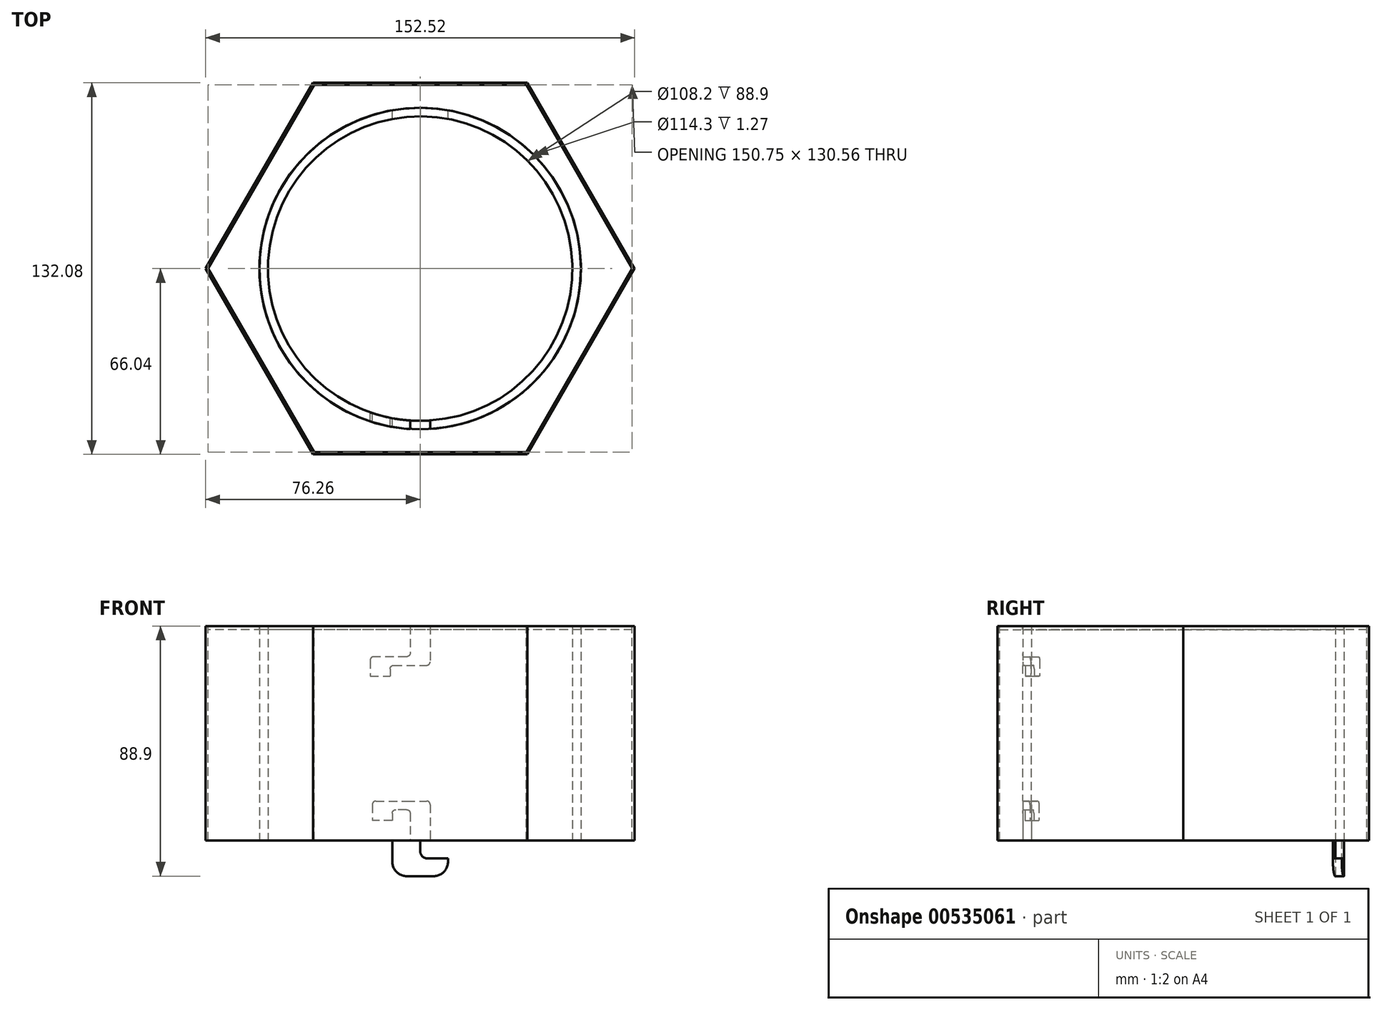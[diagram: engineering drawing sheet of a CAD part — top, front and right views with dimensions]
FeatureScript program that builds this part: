
annotation { "Feature Type Name" : "Feature", "Feature Type Description" : "" }
export const myFeature = defineFeature(function(context is Context, id is Id, definition is map)
    precondition{}
    {
        {
            var Q0;
            Q0=qCreatedBy(makeId("Top.planeOp"),FACE);
            var sketch = newSketch(context, id + "F0", { "sketchPlane" : qUnion([Q0])});
            skCircle(sketch, "E0", {"center": v(0, 0) * mm, "radius": 54.1 * mm});
            skCircle(sketch, "E1", {"center": v(0, 0) * mm, "radius": 57.15 * mm});
            skSolve(sketch);
        }
        {
            var Q0;
            Q0=qSketchRegion(id+"F0",true);
            extrude(context, id + "F1", {"entities" : qUnion([Q0]), "depth" : 76.2 * mm, "offsetDistance" : 25.4 * mm, "symmetric" : true});
        }
        {
            var Q0;
            Q0=qCreatedBy(makeId("Front.planeOp"),FACE);
            var sketch = newSketch(context, id + "F2", { "sketchPlane" : qUnion([Q0])});
            skLineSegment(sketch, "E2", {"start": v(-3.56, -38.1) * mm, "end": v(-3.56, -27.18) * mm});
            skLineSegment(sketch, "E3", {"start": v(-3.56, -27.18) * mm, "end": v(-9.9, -27.18) * mm});
            skLineSegment(sketch, "E4", {"start": v(-9.9, -27.18) * mm, "end": v(-9.9, -30.99) * mm});
            skLineSegment(sketch, "E5", {"start": v(-9.9, -30.99) * mm, "end": v(-17.02, -30.99) * mm});
            skLineSegment(sketch, "E6", {"start": v(-17.02, -30.99) * mm, "end": v(-17.02, -24.13) * mm});
            skLineSegment(sketch, "E7", {"start": v(-17.02, -24.13) * mm, "end": v(3.56, -24.13) * mm});
            skLineSegment(sketch, "E8", {"start": v(3.56, -24.13) * mm, "end": v(3.56, -38.1) * mm});
            skPoint(sketch, "E9", {"position": v(0, -38.1) * mm});
            skPoint(sketch, "E10", {"position": v(3.56, -38.1) * mm});
            skPoint(sketch, "E11", {"position": v(-3.56, -38.1) * mm});
            skLineSegment(sketch, "E12", {"start": v(-3.56, -38.1) * mm, "end": v(3.56, -38.1) * mm});
            skPoint(sketch, "E13.MirrorP", {"position": v(-3.56, 38.1) * mm});
            skLineSegment(sketch, "E14.MirrorCS", {"start": v(-3.56, 38.1) * mm, "end": v(3.56, 38.1) * mm});
            skLineSegment(sketch, "E15.MirrorCS", {"start": v(3.56, 24.13) * mm, "end": v(3.56, 38.1) * mm});
            skLineSegment(sketch, "E16.MirrorCS", {"start": v(-3.56, 38.1) * mm, "end": v(-3.56, 27.18) * mm});
            skLineSegment(sketch, "E17", {"start": v(-3.56, 27.18) * mm, "end": v(-17.78, 27.18) * mm});
            skLineSegment(sketch, "E18", {"start": v(-17.78, 27.18) * mm, "end": v(-17.78, 20.32) * mm});
            skLineSegment(sketch, "E19", {"start": v(-17.78, 20.32) * mm, "end": v(-10.67, 20.32) * mm});
            skLineSegment(sketch, "E20", {"start": v(-10.67, 20.32) * mm, "end": v(-10.67, 24.13) * mm});
            skLineSegment(sketch, "E21", {"start": v(-10.67, 24.13) * mm, "end": v(3.56, 24.13) * mm});
            skSolve(sketch);
        }
        {
            var Q0;
            Q0=qSketchRegion(id+"F2",true);
            extrude(context, id + "F3", {"entities" : qUnion([Q0]), "operationType" : NewBodyOperationType.REMOVE, "depth" : 133.86 * mm, "offsetDistance" : 25.4 * mm});
        }
        {
            var Q0;
            Q0=makeQuery(id+"F3.boolean.opBoolean","COPY",EDGE,{"derivedFrom":makeQuery(id+"F3.opExtrude","SWEPT_EDGE",EDGE,{"disambiguationData":[OSD([sQuery(id+"F2.wireOp",EDGE,"E3"),sQuery(id+"F2.wireOp",EDGE,"E4")])]})});
            var Q1;
            Q1=makeQuery(id+"F3.boolean.opBoolean","COPY",EDGE,{"derivedFrom":makeQuery(id+"F3.opExtrude","SWEPT_EDGE",EDGE,{"disambiguationData":[OSD([sQuery(id+"F2.wireOp",EDGE,"E2"),sQuery(id+"F2.wireOp",EDGE,"E3")])]})});
            var Q2;
            Q2=makeQuery(id+"F3.boolean.opBoolean","COPY",EDGE,{"derivedFrom":makeQuery(id+"F3.opExtrude","SWEPT_EDGE",EDGE,{"disambiguationData":[OSD([sQuery(id+"F2.wireOp",EDGE,"E7"),sQuery(id+"F2.wireOp",EDGE,"E8")])]})});
            var Q3;
            Q3=makeQuery(id+"F3.boolean.opBoolean","COPY",EDGE,{"derivedFrom":makeQuery(id+"F3.opExtrude","SWEPT_EDGE",EDGE,{"disambiguationData":[OSD([sQuery(id+"F2.wireOp",EDGE,"E6"),sQuery(id+"F2.wireOp",EDGE,"E7")])]})});
            fillet(context, id + "F4", {"entities" : qUnion([Q0, Q1, Q2, Q3]), "radius" : 1.27 * mm, "tangentPropagation" : true, "allowEdgeOverflow" : false});
        }
        {
            var Q0;
            Q0=makeQuery(id+"F3.boolean.opBoolean","COPY",EDGE,{"derivedFrom":makeQuery(id+"F3.opExtrude","SWEPT_EDGE",EDGE,{"disambiguationData":[OSD([sQuery(id+"F2.wireOp",EDGE,"E20"),sQuery(id+"F2.wireOp",EDGE,"E21")])]})});
            var Q1;
            Q1=makeQuery(id+"F3.boolean.opBoolean","COPY",EDGE,{"derivedFrom":makeQuery(id+"F3.opExtrude","SWEPT_EDGE",EDGE,{"disambiguationData":[OSD([sQuery(id+"F2.wireOp",EDGE,"E15.MirrorCS"),sQuery(id+"F2.wireOp",EDGE,"E21")])]})});
            var Q2;
            Q2=makeQuery(id+"F3.boolean.opBoolean","COPY",EDGE,{"derivedFrom":makeQuery(id+"F3.opExtrude","SWEPT_EDGE",EDGE,{"disambiguationData":[OSD([sQuery(id+"F2.wireOp",EDGE,"E16.MirrorCS"),sQuery(id+"F2.wireOp",EDGE,"E17")])]})});
            var Q3;
            Q3=makeQuery(id+"F3.boolean.opBoolean","COPY",EDGE,{"derivedFrom":makeQuery(id+"F3.opExtrude","SWEPT_EDGE",EDGE,{"disambiguationData":[OSD([sQuery(id+"F2.wireOp",EDGE,"E17"),sQuery(id+"F2.wireOp",EDGE,"E18")])]})});
            fillet(context, id + "F5", {"entities" : qUnion([Q0, Q1, Q2, Q3]), "radius" : 1.27 * mm, "tangentPropagation" : true, "allowEdgeOverflow" : false});
        }
        {
            var Q0;
            {var subQ0=sQuery(id+"F0.wireOp",EDGE,"E0");var subQ2=sQuery(id+"F0.wireOp",EDGE,"E1");var subQ4=makeQuery(id+"FeuOR3F4EdYcHin_1.1.F3.opExtrude","SWEPT_FACE",FACE,{"disambiguationData":[OSD([sQuery(id+"F2.wireOp",EDGE,"E2")])]});var subQ5=sQuery(id+"F2.wireOp",EDGE,"E8");Q0=makeQuery(id+"FeuOR3F4EdYcHin_1.2.F3.boolean.opBoolean","SPLIT",FACE,{"disambiguationData":[TD([makeQuery(id+"FeuOR3F4EdYcHin_1.1.F3.boolean.opBoolean","COPY",FACE,{"derivedFrom":subQ4})])],"derivedFrom":makeQuery(id+"FeuOR3F4EdYcHin_1.1.F3.boolean.opBoolean","SPLIT",FACE,{"disambiguationData":[TD([makeQuery(id+"F3.boolean.opBoolean","COPY",FACE,{"derivedFrom":makeQuery(id+"F3.opExtrude","SWEPT_FACE",FACE,{"disambiguationData":[OSD([subQ5])]})})])],"derivedFrom":makeQuery(id+"F1.opExtrude","CAP_FACE",FACE,{"disambiguationData":[OSD([subQ0,subQ2])],"isStart":true})})});}
            var sketch = newSketch(context, id + "F6", { "sketchPlane" : qUnion([Q0])});
            skLineSegment(sketch, "E22", {"start": v(-9.9, -53.19) * mm, "end": v(-9.9, -56.28) * mm});
            skLineSegment(sketch, "E23", {"start": v(9.9, -53.19) * mm, "end": v(9.9, -56.28) * mm});
            skSolve(sketch);
        }
        {
            var Q0;
            Q0=qSketchRegion(id+"F6",true);
            var Q1;
            {var subQ0=sQuery(id+"F6.wireOp",EDGE,"E22");Q1=makeQuery(id+"F6.imprint","IMPRINT",FACE,{"disambiguationData":[TD([[makeQuery(id+"F6.imprint","IMPRINT",EDGE,{"derivedFrom":subQ0}),1.0]])]});}
            extrude(context, id + "F7", {"entities" : qUnion([Q0, Q1]), "operationType" : NewBodyOperationType.ADD, "depth" : 12.7 * mm, "offsetDistance" : 25.4 * mm});
        }
        {
            var Q0;
            Q0=qCreatedBy(makeId("Front.planeOp"),FACE);
            var sketch = newSketch(context, id + "F8", { "sketchPlane" : qUnion([Q0])});
            skLineSegment(sketch, "E24", {"start": v(9.9, -38.15) * mm, "end": v(0, -38.15) * mm});
            skLineSegment(sketch, "E25", {"start": v(0, -38.15) * mm, "end": v(0, -44.5) * mm});
            skLineSegment(sketch, "E26", {"start": v(0, -44.5) * mm, "end": v(9.9, -44.5) * mm});
            skLineSegment(sketch, "E27", {"start": v(9.9, -38.15) * mm, "end": v(9.9, -44.5) * mm});
            skSolve(sketch);
        }
        {
            var Q0;
            Q0=qSketchRegion(id+"F8",true);
            extrude(context, id + "F9", {"entities" : qUnion([Q0]), "operationType" : NewBodyOperationType.REMOVE, "oppositeDirection" : true, "depth" : 73.9 * mm, "offsetDistance" : 25.4 * mm});
        }
        {
            var Q0;
            Q0=makeQuery(id+"F9.boolean.opBoolean","COPY",EDGE,{"derivedFrom":makeQuery(id+"F9.opExtrude","SWEPT_EDGE",EDGE,{"disambiguationData":[OSD([sQuery(id+"F8.wireOp",EDGE,"E25"),sQuery(id+"F8.wireOp",EDGE,"E26")])]})});
            fillet(context, id + "F10", {"entities" : qUnion([Q0]), "radius" : 2.54 * mm, "tangentPropagation" : true, "allowEdgeOverflow" : false});
        }
        {
            var Q0;
            Q0=makeQuery(id+"F7.opExtrude","CAP_EDGE",EDGE,{"disambiguationData":[OSD([sQuery(id+"F6.wireOp",EDGE,"E23")])],"isStart":false});
            var Q1;
            Q1=makeQuery(id+"F7.opExtrude","CAP_EDGE",EDGE,{"disambiguationData":[OSD([sQuery(id+"F6.wireOp",EDGE,"E22")])],"isStart":false});
            fillet(context, id + "F11", {"entities" : qUnion([Q0, Q1]), "radius" : 5.08 * mm, "tangentPropagation" : true, "allowEdgeOverflow" : false});
        }
        {
            var Q0;
            {var subQ0=sQuery(id+"F0.wireOp",EDGE,"E0");var subQ1=sQuery(id+"F0.wireOp",EDGE,"E1");Q0=makeQuery(id+"FeuOR3F4EdYcHin_1.1.F3.boolean.opBoolean","SPLIT",FACE,{"disambiguationData":[TD([makeQuery(id+"F3.boolean.opBoolean","COPY",FACE,{"derivedFrom":makeQuery(id+"F3.opExtrude","SWEPT_FACE",FACE,{"disambiguationData":[OSD([sQuery(id+"F2.wireOp",EDGE,"E16.MirrorCS")])]})})])],"derivedFrom":makeQuery(id+"F1.opExtrude","CAP_FACE",FACE,{"disambiguationData":[OSD([subQ0,subQ1])],"isStart":false})});}
            var sketch = newSketch(context, id + "F12", { "sketchPlane" : qUnion([Q0])});
            skCircle(sketch, "E28.cCircle", {"center": v(0, 0) * mm, "radius": 66.04 * mm, "construction": true});
            skLineSegment(sketch, "E28.0", {"start": v(-38.13, -66.04) * mm, "end": v(-76.26, 0) * mm});
            skLineSegment(sketch, "E28.1", {"start": v(-76.26, 0) * mm, "end": v(-38.13, 66.04) * mm});
            skLineSegment(sketch, "E28.2", {"start": v(-38.13, 66.04) * mm, "end": v(38.13, 66.04) * mm});
            skLineSegment(sketch, "E28.3", {"start": v(38.13, 66.04) * mm, "end": v(76.26, 0) * mm});
            skLineSegment(sketch, "E28.4", {"start": v(76.26, 0) * mm, "end": v(38.13, -66.04) * mm});
            skLineSegment(sketch, "E28.5", {"start": v(38.13, -66.04) * mm, "end": v(-38.13, -66.04) * mm});
            skPoint(sketch, "E28.0.midPoint", {"position": v(-57.2, -33.02) * mm});
            skCircle(sketch, "E29.cCircle", {"center": v(0, 0) * mm, "radius": 65.28 * mm, "construction": true});
            skLineSegment(sketch, "E29.0", {"start": v(-37.69, -65.28) * mm, "end": v(-75.38, 0) * mm});
            skLineSegment(sketch, "E29.1", {"start": v(-75.38, 0) * mm, "end": v(-37.69, 65.28) * mm});
            skLineSegment(sketch, "E29.2", {"start": v(-37.69, 65.28) * mm, "end": v(37.69, 65.28) * mm});
            skLineSegment(sketch, "E29.3", {"start": v(37.69, 65.28) * mm, "end": v(75.38, 0) * mm});
            skLineSegment(sketch, "E29.4", {"start": v(75.38, 0) * mm, "end": v(37.69, -65.28) * mm});
            skLineSegment(sketch, "E29.5", {"start": v(37.69, -65.28) * mm, "end": v(-37.69, -65.28) * mm});
            skPoint(sketch, "E29.0.midPoint", {"position": v(-56.53, -32.64) * mm});
            skCircle(sketch, "E30", {"center": v(0, 0) * mm, "radius": 57.15 * mm});
            skSolve(sketch);
        }
        {
            var Q0;
            Q0 = qSketchRegion(id + "F12", true);
            extrude(context, id + "F13", {"entities" : qUnion([Q0]), "oppositeDirection" : true, "depth" : 76.2 * mm, "offsetDistance" : 25.4 * mm});
        }
        {
            var Q0;
            {var subQ0=sQuery(id+"F0.wireOp",EDGE,"E0");var subQ1=sQuery(id+"F0.wireOp",EDGE,"E1");Q0=makeQuery(id+"FeuOR3F4EdYcHin_1.1.F3.boolean.opBoolean","SPLIT",FACE,{"disambiguationData":[TD([makeQuery(id+"F3.boolean.opBoolean","COPY",FACE,{"derivedFrom":makeQuery(id+"F3.opExtrude","SWEPT_FACE",FACE,{"disambiguationData":[OSD([sQuery(id+"F2.wireOp",EDGE,"E16.MirrorCS")])]})})])],"derivedFrom":makeQuery(id+"F1.opExtrude","CAP_FACE",FACE,{"disambiguationData":[OSD([subQ0,subQ1])],"isStart":false})});}
            var sketch = newSketch(context, id + "F14", { "sketchPlane" : qUnion([Q0])});
            skSolve(sketch);
        }
        {
            var Q0;
            Q0=makeQuery(id+"F12.imprint","IMPRINT",FACE,{"disambiguationData":[TD([[makeQuery(id+"F12.imprint","IMPRINT",EDGE,{"derivedFrom":sQuery(id+"F12.wireOp",EDGE,"E29.0")}),-1.0]])]});
            extrude(context, id + "F15", {"entities" : qUnion([Q0]), "oppositeDirection" : true, "depth" : 1.27 * mm, "offsetDistance" : 25.4 * mm});
        }
    });
